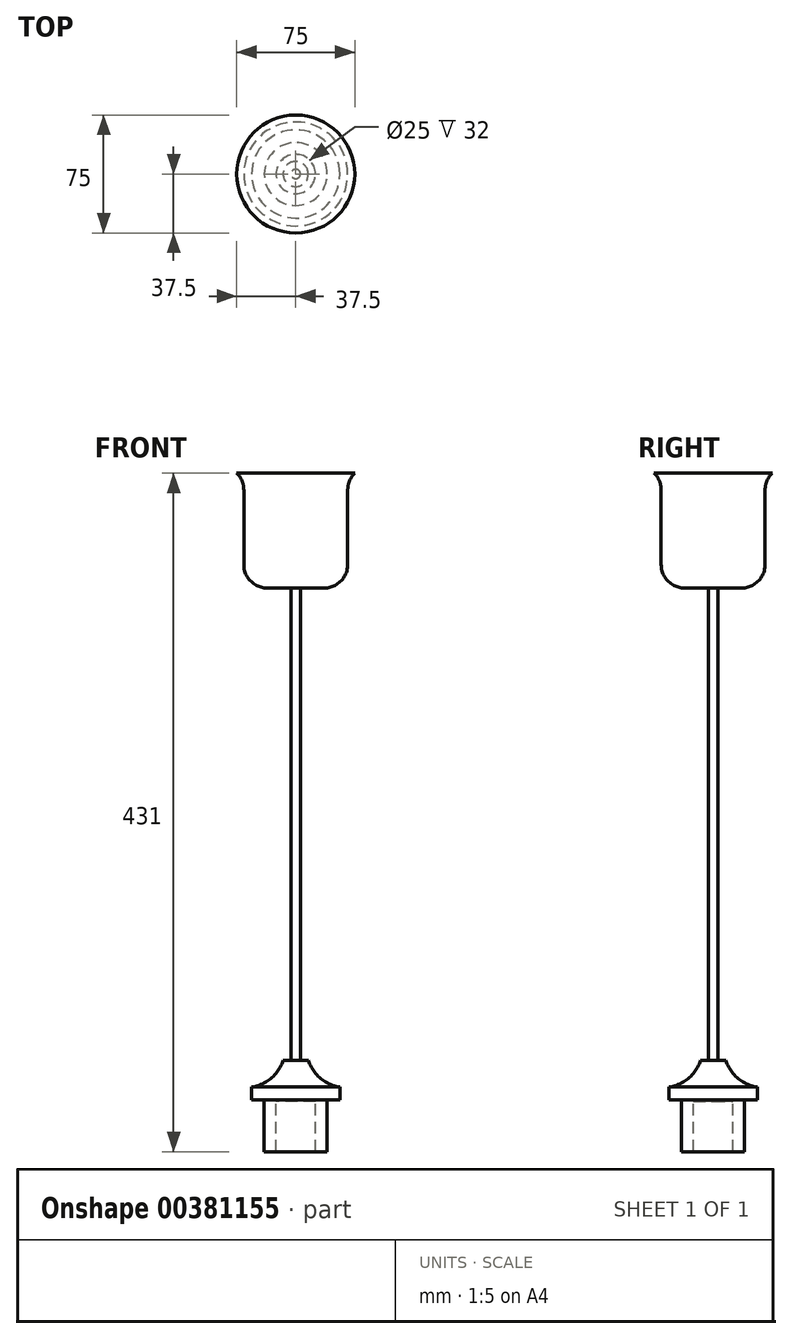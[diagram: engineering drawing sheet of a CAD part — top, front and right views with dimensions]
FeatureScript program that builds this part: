
annotation { "Feature Type Name" : "Feature", "Feature Type Description" : "" }
export const myFeature = defineFeature(function(context is Context, id is Id, definition is map)
    precondition{}
    {
        {
            var Q0;
            Q0=qCreatedBy(makeId("Front.planeOp"),FACE);
            var sketch = newSketch(context, id + "F0", { "sketchPlane" : qUnion([Q0])});
            skLineSegment(sketch, "E0", {"start": v(0, 32) * mm, "end": v(12.5, 32) * mm});
            skLineSegment(sketch, "E1", {"start": v(12.5, 32) * mm, "end": v(12.5, 0) * mm});
            skLineSegment(sketch, "E2", {"start": v(12.5, 0) * mm, "end": v(20, 0) * mm});
            skLineSegment(sketch, "E3", {"start": v(20, 0) * mm, "end": v(20, 33) * mm});
            skLineSegment(sketch, "E4", {"start": v(20, 33) * mm, "end": v(28, 33) * mm});
            skLineSegment(sketch, "E5", {"start": v(28, 33) * mm, "end": v(28, 41) * mm});
            skLineSegment(sketch, "E6", {"start": v(3, 58) * mm, "end": v(8, 58) * mm});
            skLineSegment(sketch, "E7", {"start": v(0, 0) * mm, "end": v(0, 50.45) * mm, "construction": true});
            skArc(sketch, "E8", {"start": v(8, 58) * mm, "mid": v(15.59, 46.66) * mm, "end": v(28, 41) * mm});
            skLineSegment(sketch, "E9", {"start": v(3, 58) * mm, "end": v(3, 358) * mm});
            skLineSegment(sketch, "E10", {"start": v(3, 358) * mm, "end": v(18, 358) * mm});
            skArc(sketch, "E11", {"start": v(18, 358) * mm, "mid": v(28.6, 362.4) * mm, "end": v(33, 373) * mm});
            skLineSegment(sketch, "E12", {"start": v(33, 373) * mm, "end": v(33, 420.29) * mm});
            skLineSegment(sketch, "E13", {"start": v(37.5, 431) * mm, "end": v(0, 431) * mm});
            skLineSegment(sketch, "E14", {"start": v(0, 431) * mm, "end": v(0, 32) * mm});
            skArc(sketch, "E15", {"start": v(37.5, 431) * mm, "mid": v(34.17, 426.1) * mm, "end": v(33, 420.29) * mm});
            skSolve(sketch);
        }
        {
            var Q0;
            Q0=qSketchRegion(id+"F0",true);
            var Q1;
            Q1=sQuery(id+"F0.wireOp",EDGE,"E14");
            revolve(context, id + "F1", {"surfaceOperationType" : NewSurfaceOperationType.NEW, "entities" : qUnion([Q0]), "axis" : qUnion([Q1]), "revolveType" : RevolveType.FULL});
        }
    });
